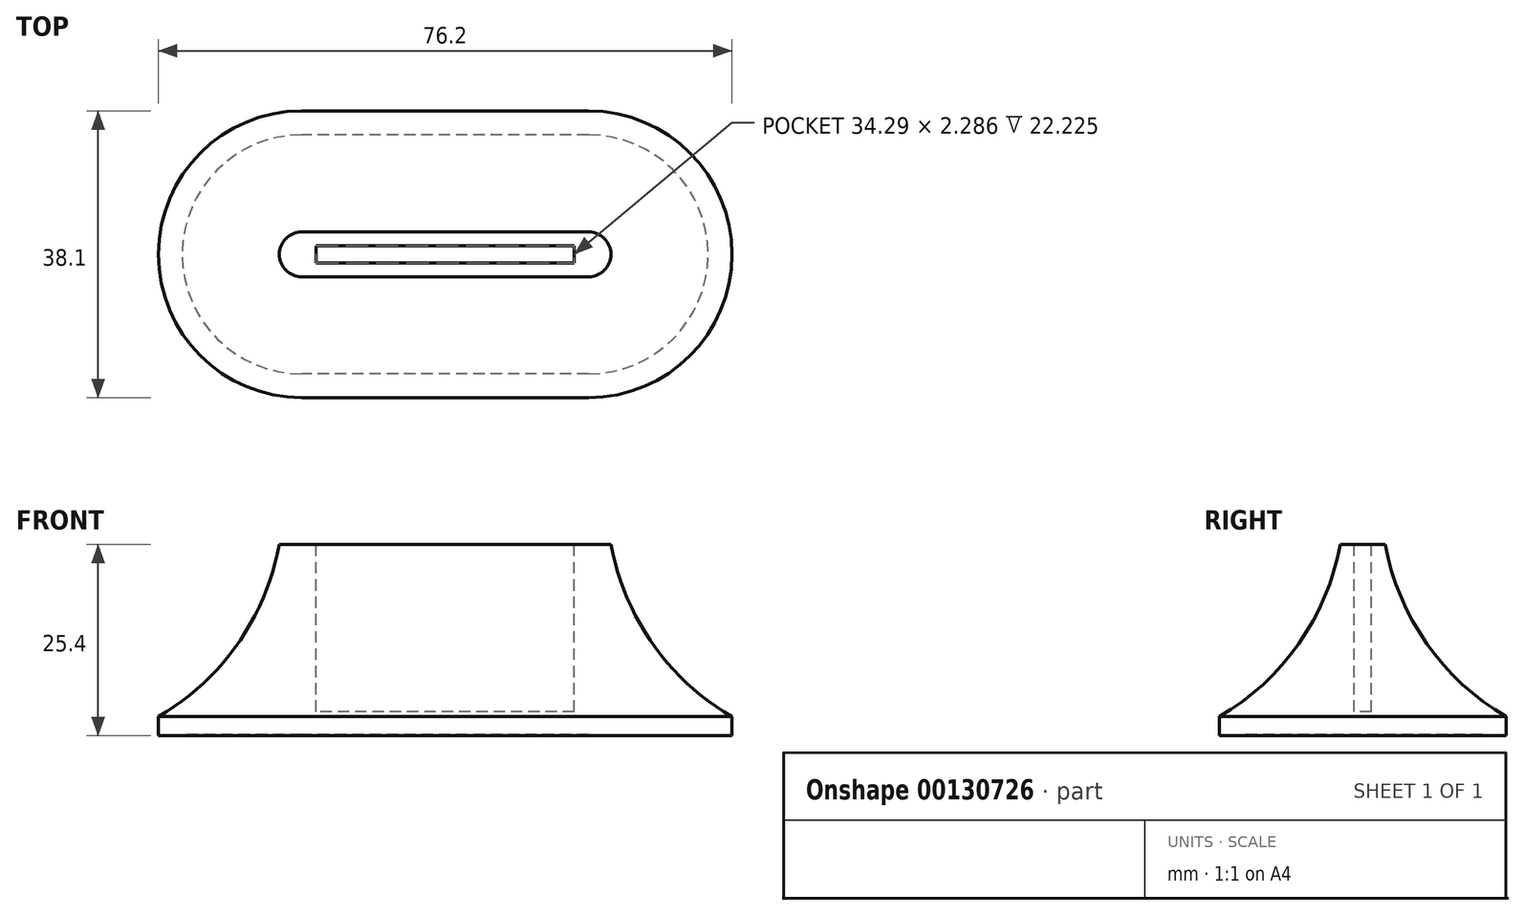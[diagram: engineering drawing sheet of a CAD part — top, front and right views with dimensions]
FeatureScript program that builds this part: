
annotation { "Feature Type Name" : "Feature", "Feature Type Description" : "" }
export const myFeature = defineFeature(function(context is Context, id is Id, definition is map)
    precondition{}
    {
        {
            var Q0;
            Q0=qCreatedBy(makeId("Top.planeOp"),FACE);
            var sketch = newSketch(context, id + "F0", { "sketchPlane" : qUnion([Q0])});
            skLineSegment(sketch, "E0.bottom", {"start": v(0, 19.05) * mm, "end": v(-19.05, 19.05) * mm});
            skLineSegment(sketch, "E0.top", {"start": v(0, -19.05) * mm, "end": v(-19.05, -19.05) * mm});
            skPoint(sketch, "E0.middle", {"position": v(0, 0) * mm});
            skLineSegment(sketch, "E1", {"start": v(0, 19.05) * mm, "end": v(0, -19.05) * mm});
            skPoint(sketch, "E0.left.start.orphan", {"position": v(36.15, 19.05) * mm});
            skPoint(sketch, "E2.orphan", {"position": v(36.15, -19.05) * mm});
            skArc(sketch, "E3", {"start": v(-19.05, 19.05) * mm, "mid": v(-38.1, 0) * mm, "end": v(-19.05, -19.05) * mm});
            skPoint(sketch, "E4.orphan", {"position": v(-36.15, -19.05) * mm});
            skPoint(sketch, "E5.orphan", {"position": v(-36.15, 19.05) * mm});
            skSolve(sketch);
        }
        {
            var Q0;
            Q0 = qSketchRegion(id + "F0", true);
            extrude(context, id + "F1", {"entities" : qUnion([Q0]), "depth" : 25.4 * mm});
        }
        {
            var Q0;
            Q0=qCreatedBy(makeId("Right.planeOp"),FACE);
            var sketch = newSketch(context, id + "F2", { "sketchPlane" : qUnion([Q0])});
            skCircle(sketch, "E6", {"center": v(-35.95, 31.46) * mm, "radius": 33.52 * mm});
            skSolve(sketch);
        }
        {
            var Q0;
            Q0=makeQuery(id+"F2.imprint","IMPRINT",FACE,{"disambiguationData":[TD([[makeQuery(id+"F2.imprint","IMPRINT",EDGE,{"derivedFrom":sQuery(id+"F2.wireOp",EDGE,"E6")}),1.0]])]});
            var Q1;
            Q1=makeQuery(id+"F1.opExtrude","CAP_EDGE",EDGE,{"disambiguationData":[OSD([sQuery(id+"F0.wireOp",EDGE,"E0.top")])],"isStart":false});
            var Q2;
            Q2=makeQuery(id+"F1.opExtrude","CAP_EDGE",EDGE,{"disambiguationData":[OSD([sQuery(id+"F0.wireOp",EDGE,"E3")])],"isStart":false});
            var Q3;
            Q3=makeQuery(id+"F1.opExtrude","CAP_EDGE",EDGE,{"disambiguationData":[OSD([sQuery(id+"F0.wireOp",EDGE,"E0.bottom")])],"isStart":false});
            sweep(context, id + "F3", {"operationType" : NewBodyOperationType.REMOVE, "profiles" : qUnion([Q0]), "path" : qUnion([Q1, Q2, Q3])});
        }
        {
            var Q0;
            Q0=makeQuery(id+"F1.opExtrude","SWEPT_BODY",BODY,{"disambiguationData":[OSD([sQuery(id+"F0.wireOp",EDGE,"E0.bottom"),sQuery(id+"F0.wireOp",EDGE,"E0.top"),sQuery(id+"F0.wireOp",EDGE,"E1"),sQuery(id+"F0.wireOp",EDGE,"E3")])]});
            var Q1;
            Q1=makeQuery(id+"F1.opExtrude","SWEPT_FACE",FACE,{"disambiguationData":[OSD([sQuery(id+"F0.wireOp",EDGE,"E1")])]});
            mirror(context, id + "F4", {"operationType" : NewBodyOperationType.ADD, "entities" : qUnion([Q0]), "mirrorPlane" : qUnion([Q1])});
        }
        {
            var Q0;
            {var subQ0=makeQuery(id+"F1.opExtrude","CAP_FACE",FACE,{"disambiguationData":[OSD([sQuery(id+"F0.wireOp",EDGE,"E0.bottom"),sQuery(id+"F0.wireOp",EDGE,"E0.top"),sQuery(id+"F0.wireOp",EDGE,"E1"),sQuery(id+"F0.wireOp",EDGE,"E3")])],"isStart":false});Q0=makeQuery(id+"F4.boolean.opBoolean","MERGE",FACE,{"derivedFrom":[subQ0,makeQuery(id+"F4.opPattern","COPY",FACE,{"derivedFrom":subQ0,"instanceName":"1"})]});}
            var sketch = newSketch(context, id + "F5", { "sketchPlane" : qUnion([Q0])});
            skLineSegment(sketch, "E7.bottom", {"start": v(17.15, 1.14) * mm, "end": v(-17.15, 1.14) * mm});
            skLineSegment(sketch, "E7.top", {"start": v(17.15, -1.14) * mm, "end": v(-17.15, -1.14) * mm});
            skLineSegment(sketch, "E7.left", {"start": v(17.15, 1.14) * mm, "end": v(17.15, -1.14) * mm});
            skLineSegment(sketch, "E7.right", {"start": v(-17.15, 1.14) * mm, "end": v(-17.15, -1.14) * mm});
            skPoint(sketch, "E7.middle", {"position": v(0, 0) * mm});
            skSolve(sketch);
        }
        {
            var Q0;
            Q0 = qSketchRegion(id + "F5", true);
            extrude(context, id + "F6", {"entities" : qUnion([Q0]), "operationType" : NewBodyOperationType.REMOVE, "oppositeDirection" : true, "depth" : 22.22 * mm});
        }
        {
            var Q0;
            {var subQ0=makeQuery(id+"F1.opExtrude","CAP_FACE",FACE,{"disambiguationData":[OSD([sQuery(id+"F0.wireOp",EDGE,"E0.bottom"),sQuery(id+"F0.wireOp",EDGE,"E0.top"),sQuery(id+"F0.wireOp",EDGE,"E1"),sQuery(id+"F0.wireOp",EDGE,"E3")])],"isStart":true});Q0=makeQuery(id+"F4.boolean.opBoolean","MERGE",FACE,{"derivedFrom":[subQ0,makeQuery(id+"F4.opPattern","COPY",FACE,{"derivedFrom":subQ0,"instanceName":"1"})]});}
            var sketch = newSketch(context, id + "F7", { "sketchPlane" : qUnion([Q0])});
            skLineSegment(sketch, "E8.0", {"start": v(19.05, 15.87) * mm, "end": v(-19.05, 15.87) * mm});
            skArc(sketch, "E8.1", {"start": v(19.05, 15.88) * mm, "mid": v(34.93, 0) * mm, "end": v(19.05, -15.88) * mm});
            skLineSegment(sketch, "E8.2", {"start": v(19.05, -15.87) * mm, "end": v(-19.05, -15.87) * mm});
            skArc(sketch, "E8.3", {"start": v(-19.05, -15.88) * mm, "mid": v(-34.93, 0) * mm, "end": v(-19.05, 15.88) * mm});
            skSolve(sketch);
        }
        {
            var Q0;
            Q0 = qSketchRegion(id + "F7", true);
            extrude(context, id + "F8", {"entities" : qUnion([Q0]), "operationType" : NewBodyOperationType.REMOVE, "oppositeDirection" : true, "depth" : 0.15 * mm});
        }
    });
